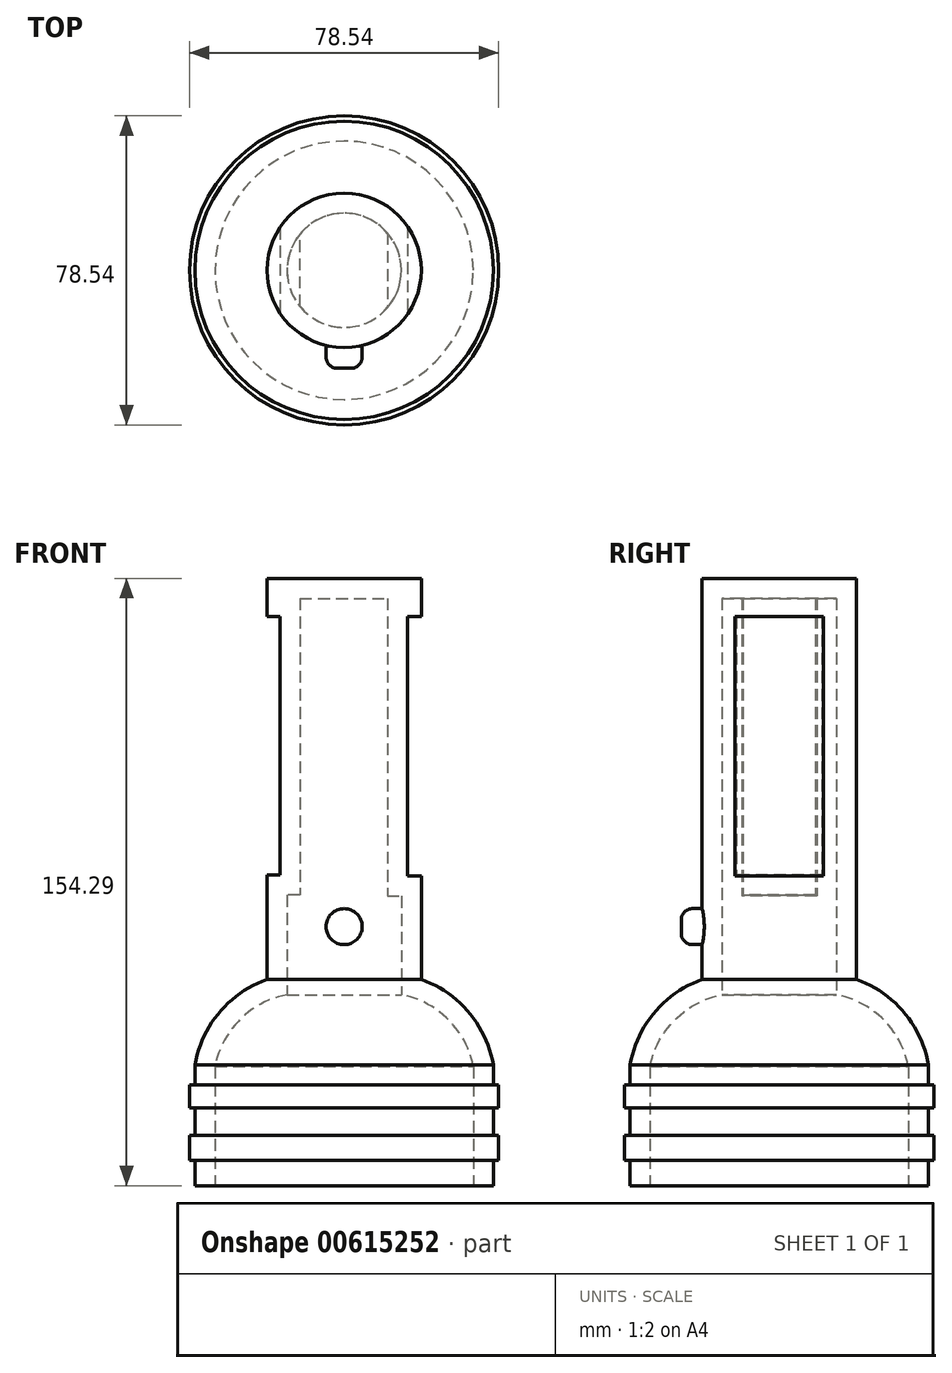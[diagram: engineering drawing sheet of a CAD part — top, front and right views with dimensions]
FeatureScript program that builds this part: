
annotation { "Feature Type Name" : "Feature", "Feature Type Description" : "" }
export const myFeature = defineFeature(function(context is Context, id is Id, definition is map)
    precondition{}
    {
        {
            var Q0;
            Q0=qCreatedBy(makeId("Front.planeOp"),FACE);
            var sketch = newSketch(context, id + "F0", { "sketchPlane" : qUnion([Q0])});
            skLineSegment(sketch, "E0", {"start": v(0, -97.36) * mm, "end": v(0, 56.93) * mm});
            skLineSegment(sketch, "E1", {"start": v(0, 56.93) * mm, "end": v(-19.6, 56.93) * mm});
            skLineSegment(sketch, "E2", {"start": v(-19.6, 56.93) * mm, "end": v(-19.6, -44.98) * mm});
            skArc(sketch, "E3", {"start": v(-19.6, -44.98) * mm, "mid": v(-31.68, -53.33) * mm, "end": v(-37.9, -66.64) * mm});
            skLineSegment(sketch, "E4", {"start": v(-37.9, -66.64) * mm, "end": v(-37.9, -71.77) * mm});
            skLineSegment(sketch, "E5", {"start": v(0, -97.36) * mm, "end": v(-37.9, -97.36) * mm});
            skLineSegment(sketch, "E6", {"start": v(-37.9, -90.97) * mm, "end": v(-37.9, -97.36) * mm});
            skLineSegment(sketch, "E7.bottom", {"start": v(-37.9, -84.55) * mm, "end": v(-39.27, -84.55) * mm});
            skLineSegment(sketch, "E7.top", {"start": v(-37.9, -90.97) * mm, "end": v(-39.27, -90.97) * mm});
            skLineSegment(sketch, "E7.right", {"start": v(-39.27, -84.55) * mm, "end": v(-39.27, -90.97) * mm});
            skPoint(sketch, "E8.oppositeSnap0", {"position": v(-39.27, -87.76) * mm});
            skLineSegment(sketch, "E8.bottom", {"start": v(-37.9, -71.77) * mm, "end": v(-39.27, -71.77) * mm});
            skLineSegment(sketch, "E8.top", {"start": v(-37.9, -77.64) * mm, "end": v(-39.27, -77.64) * mm});
            skLineSegment(sketch, "E8.right", {"start": v(-39.27, -71.77) * mm, "end": v(-39.27, -77.64) * mm});
            skLineSegment(sketch, "E9.trimOffspring", {"start": v(-37.9, -77.64) * mm, "end": v(-37.9, -84.55) * mm});
            skSolve(sketch);
        }
        {
            var Q0;
            Q0=makeQuery(id+"F0.imprint","IMPRINT",FACE,{"disambiguationData":[TD([[makeQuery(id+"F0.imprint","IMPRINT",EDGE,{"derivedFrom":sQuery(id+"F0.wireOp",EDGE,"E0")}),1.0]])]});
            var Q1;
            Q1=sQuery(id+"F0.wireOp",EDGE,"E0");
            revolve(context, id + "F1", {"entities" : qUnion([Q0]), "axis" : qUnion([Q1]), "revolveType" : RevolveType.FULL});
        }
        {
            var Q0;
            Q0=qCreatedBy(makeId("Front.planeOp"),FACE);
            var sketch = newSketch(context, id + "F2", { "sketchPlane" : qUnion([Q0])});
            skCircle(sketch, "E10", {"center": v(0, -31.54) * mm, "radius": 4.58 * mm});
            skSolve(sketch);
        }
        {
            var Q0;
            Q0 = qSketchRegion(id + "F2", true);
            extrude(context, id + "F3", {"entities" : qUnion([Q0]), "operationType" : NewBodyOperationType.ADD, "depth" : 24.9 * mm, "offsetDistance" : 25.4 * mm});
        }
        {
            var Q0;
            Q0=makeQuery(id+"F3.opExtrude","CAP_EDGE",EDGE,{"disambiguationData":[OSD([sQuery(id+"F2.wireOp",EDGE,"E10")])],"isStart":false});
            fillet(context, id + "F4", {"entities" : qUnion([Q0]), "radius" : 2.82 * mm, "tangentPropagation" : true, "allowEdgeOverflow" : false});
        }
        {
            var Q0;
            Q0=qCreatedBy(makeId("Front.planeOp"),FACE);
            var sketch = newSketch(context, id + "F5", { "sketchPlane" : qUnion([Q0])});
            skLineSegment(sketch, "E11.bottom", {"start": v(-27.03, 47.2) * mm, "end": v(-16.33, 47.2) * mm});
            skLineSegment(sketch, "E11.top", {"start": v(-27.03, -18.4) * mm, "end": v(-16.33, -18.4) * mm});
            skLineSegment(sketch, "E11.left", {"start": v(-27.03, 47.2) * mm, "end": v(-27.03, -18.4) * mm});
            skLineSegment(sketch, "E11.right", {"start": v(-16.33, 47.2) * mm, "end": v(-16.33, -18.4) * mm});
            skPoint(sketch, "E12.firstSnap0", {"position": v(-21.68, 47.2) * mm});
            skLineSegment(sketch, "E12.bottom", {"start": v(16.06, 47.2) * mm, "end": v(32.52, 47.2) * mm});
            skLineSegment(sketch, "E12.top", {"start": v(16.06, -18.68) * mm, "end": v(32.52, -18.68) * mm});
            skLineSegment(sketch, "E12.left", {"start": v(16.06, 47.2) * mm, "end": v(16.06, -18.68) * mm});
            skLineSegment(sketch, "E12.right", {"start": v(32.52, 47.2) * mm, "end": v(32.52, -18.68) * mm});
            skSolve(sketch);
        }
        {
            var Q0;
            Q0 = qSketchRegion(id + "F5", true);
            extrude(context, id + "F6", {"entities" : qUnion([Q0]), "operationType" : NewBodyOperationType.REMOVE, "endBound" : BoundingType.SYMMETRIC, "oppositeDirection" : true, "depth" : 39.12 * mm, "offsetDistance" : 25.4 * mm});
        }
        {
            var Q0;
            Q0=makeQuery(id+"F1.opRevolve","SWEPT_FACE",FACE,{"disambiguationData":[OSD([sQuery(id+"F0.wireOp",EDGE,"E5")])]});
            shell(context, id + "F7", {"entities" : qUnion([Q0]), "thickness" : 5.08 * mm});
        }
    });
